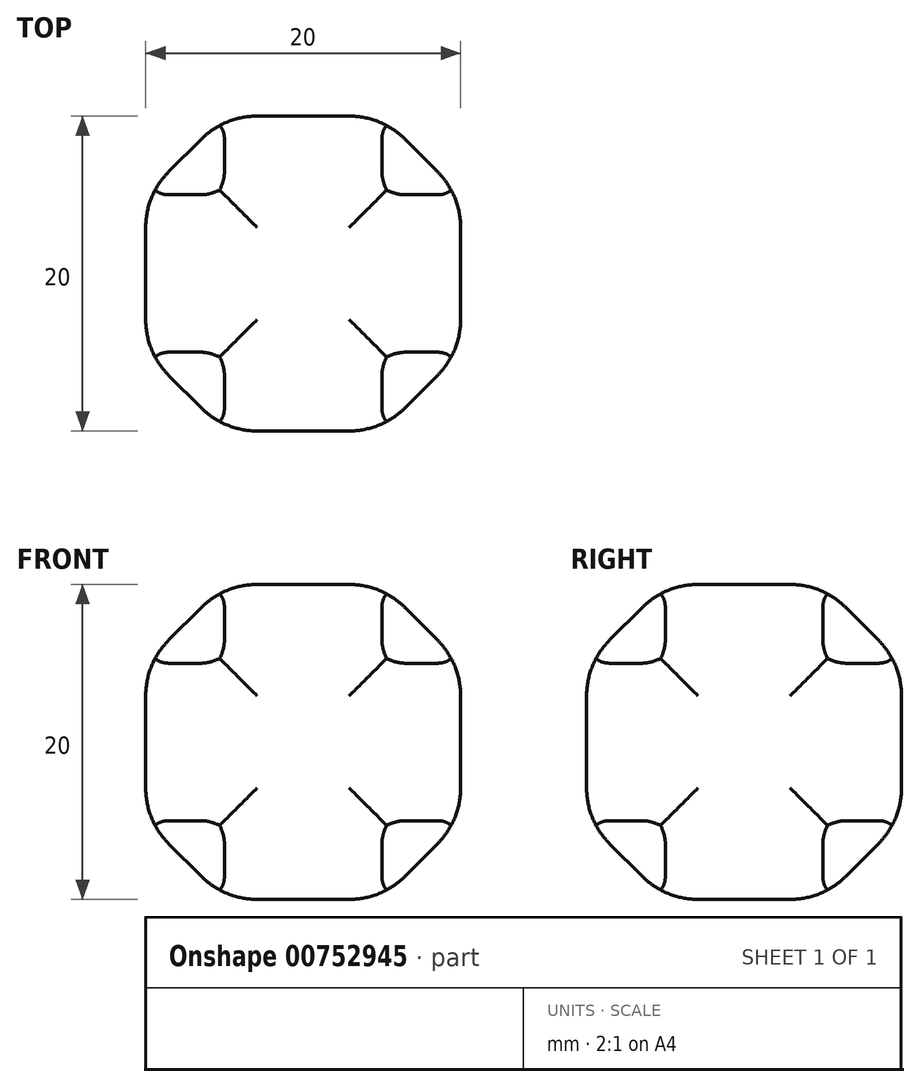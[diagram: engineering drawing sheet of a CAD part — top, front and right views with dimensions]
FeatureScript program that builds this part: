
annotation { "Feature Type Name" : "Feature", "Feature Type Description" : "" }
export const myFeature = defineFeature(function(context is Context, id is Id, definition is map)
    precondition{}
    {
        {
            var Q0;
            Q0=qCreatedBy(makeId("Top.planeOp"),FACE);
            var sketch = newSketch(context, id + "F0", { "sketchPlane" : qUnion([Q0])});
            skLineSegment(sketch, "E0.bottom", {"start": v(-1.4, 9.82) * mm, "end": v(18.6, 9.82) * mm});
            skLineSegment(sketch, "E0.top", {"start": v(-1.4, -10.18) * mm, "end": v(18.6, -10.18) * mm});
            skLineSegment(sketch, "E0.left", {"start": v(-1.4, 9.82) * mm, "end": v(-1.4, -10.18) * mm});
            skLineSegment(sketch, "E0.right", {"start": v(18.6, 9.82) * mm, "end": v(18.6, -10.18) * mm});
            skSolve(sketch);
        }
        {
            var Q0;
            Q0=makeQuery(id+"F0.imprint","IMPRINT",FACE,{"disambiguationData":[TD([[makeQuery(id+"F0.imprint","IMPRINT",EDGE,{"derivedFrom":sQuery(id+"F0.wireOp",EDGE,"E0.bottom")}),-1.0]])]});
            extrude(context, id + "F1", {"entities" : qUnion([Q0]), "depth" : 20 * mm, "offsetDistance" : 25 * mm});
        }
        {
            var Q0;
            Q0=makeQuery(id+"F1.opExtrude","CAP_EDGE",EDGE,{"disambiguationData":[OSD([sQuery(id+"F0.wireOp",EDGE,"E0.top")])],"isStart":false});
            var Q1;
            Q1=makeQuery(id+"F1.opExtrude","CAP_EDGE",EDGE,{"disambiguationData":[OSD([sQuery(id+"F0.wireOp",EDGE,"E0.right")])],"isStart":false});
            var Q2;
            Q2=makeQuery(id+"F1.opExtrude","CAP_EDGE",EDGE,{"disambiguationData":[OSD([sQuery(id+"F0.wireOp",EDGE,"E0.bottom")])],"isStart":false});
            var Q3;
            Q3=makeQuery(id+"F1.opExtrude","CAP_EDGE",EDGE,{"disambiguationData":[OSD([sQuery(id+"F0.wireOp",EDGE,"E0.left")])],"isStart":false});
            var Q4;
            Q4=makeQuery(id+"F1.opExtrude","CAP_EDGE",EDGE,{"disambiguationData":[OSD([sQuery(id+"F0.wireOp",EDGE,"E0.left")])],"isStart":true});
            var Q5;
            Q5=makeQuery(id+"F1.opExtrude","CAP_EDGE",EDGE,{"disambiguationData":[OSD([sQuery(id+"F0.wireOp",EDGE,"E0.bottom")])],"isStart":true});
            var Q6;
            Q6=makeQuery(id+"F1.opExtrude","CAP_EDGE",EDGE,{"disambiguationData":[OSD([sQuery(id+"F0.wireOp",EDGE,"E0.right")])],"isStart":true});
            var Q7;
            Q7=makeQuery(id+"F1.opExtrude","CAP_EDGE",EDGE,{"disambiguationData":[OSD([sQuery(id+"F0.wireOp",EDGE,"E0.top")])],"isStart":true});
            var Q8;
            Q8=makeQuery(id+"F1.opExtrude","SWEPT_EDGE",EDGE,{"disambiguationData":[OSD([sQuery(id+"F0.wireOp",EDGE,"E0.bottom"),sQuery(id+"F0.wireOp",EDGE,"E0.left")])]});
            var Q9;
            Q9=makeQuery(id+"F1.opExtrude","SWEPT_EDGE",EDGE,{"disambiguationData":[OSD([sQuery(id+"F0.wireOp",EDGE,"E0.bottom"),sQuery(id+"F0.wireOp",EDGE,"E0.right")])]});
            var Q10;
            Q10=makeQuery(id+"F1.opExtrude","SWEPT_EDGE",EDGE,{"disambiguationData":[OSD([sQuery(id+"F0.wireOp",EDGE,"E0.top"),sQuery(id+"F0.wireOp",EDGE,"E0.right")])]});
            var Q11;
            Q11=makeQuery(id+"F1.opExtrude","SWEPT_EDGE",EDGE,{"disambiguationData":[OSD([sQuery(id+"F0.wireOp",EDGE,"E0.top"),sQuery(id+"F0.wireOp",EDGE,"E0.left")])]});
            chamfer(context, id + "F2", {"entities" : qUnion([Q0, Q1, Q2, Q3, Q4, Q5, Q6, Q7, Q8, Q9, Q10, Q11]), "width" : 5 * mm, "tangentPropagation" : true});
        }
        {
            var Q0;
            {var subQ0=sQuery(id+"F0.wireOp",EDGE,"E0.right");Q0=makeQuery(id+"F2.opChamfer","BLEND_EDGE",EDGE,{"blendedFrom":[makeQuery(id+"F1.opExtrude","CAP_EDGE",EDGE,{"disambiguationData":[OSD([subQ0])],"isStart":true}),makeQuery(id+"F1.opExtrude","CAP_FACE",FACE,{"disambiguationData":[OSD([sQuery(id+"F0.wireOp",EDGE,"E0.bottom"),sQuery(id+"F0.wireOp",EDGE,"E0.top"),sQuery(id+"F0.wireOp",EDGE,"E0.left"),subQ0])],"isStart":true})],"blendedInto":[makeQuery(id+"F1.opExtrude","CAP_FACE",FACE,{"disambiguationData":[OSD([sQuery(id+"F0.wireOp",EDGE,"E0.bottom"),sQuery(id+"F0.wireOp",EDGE,"E0.top"),sQuery(id+"F0.wireOp",EDGE,"E0.left"),subQ0])],"isStart":true})]});}
            var Q1;
            {var subQ0=sQuery(id+"F0.wireOp",EDGE,"E0.right");Q1=makeQuery(id+"F2.opChamfer","BLEND_EDGE",EDGE,{"blendedFrom":[makeQuery(id+"F1.opExtrude","CAP_EDGE",EDGE,{"disambiguationData":[OSD([subQ0])],"isStart":true}),makeQuery(id+"F1.opExtrude","SWEPT_FACE",FACE,{"disambiguationData":[OSD([subQ0])]})],"blendedInto":[makeQuery(id+"F1.opExtrude","SWEPT_FACE",FACE,{"disambiguationData":[OSD([subQ0])]})]});}
            var Q2;
            {var subQ0=sQuery(id+"F0.wireOp",EDGE,"E0.right");Q2=makeQuery(id+"F2.opChamfer","BLEND_EDGE",EDGE,{"blendedFrom":[makeQuery(id+"F1.opExtrude","CAP_EDGE",EDGE,{"disambiguationData":[OSD([subQ0])],"isStart":false}),makeQuery(id+"F1.opExtrude","SWEPT_FACE",FACE,{"disambiguationData":[OSD([subQ0])]})],"blendedInto":[makeQuery(id+"F1.opExtrude","SWEPT_FACE",FACE,{"disambiguationData":[OSD([subQ0])]})]});}
            var Q3;
            {var subQ0=sQuery(id+"F0.wireOp",EDGE,"E0.right");Q3=makeQuery(id+"F2.opChamfer","BLEND_EDGE",EDGE,{"blendedFrom":[makeQuery(id+"F1.opExtrude","CAP_EDGE",EDGE,{"disambiguationData":[OSD([subQ0])],"isStart":false}),makeQuery(id+"F1.opExtrude","CAP_FACE",FACE,{"disambiguationData":[OSD([sQuery(id+"F0.wireOp",EDGE,"E0.bottom"),sQuery(id+"F0.wireOp",EDGE,"E0.top"),sQuery(id+"F0.wireOp",EDGE,"E0.left"),subQ0])],"isStart":false})],"blendedInto":[makeQuery(id+"F1.opExtrude","CAP_FACE",FACE,{"disambiguationData":[OSD([sQuery(id+"F0.wireOp",EDGE,"E0.bottom"),sQuery(id+"F0.wireOp",EDGE,"E0.top"),sQuery(id+"F0.wireOp",EDGE,"E0.left"),subQ0])],"isStart":false})]});}
            var Q4;
            {var subQ0=sQuery(id+"F0.wireOp",EDGE,"E0.left");Q4=makeQuery(id+"F2.opChamfer","BLEND_EDGE",EDGE,{"blendedFrom":[makeQuery(id+"F1.opExtrude","CAP_EDGE",EDGE,{"disambiguationData":[OSD([subQ0])],"isStart":false}),makeQuery(id+"F1.opExtrude","CAP_FACE",FACE,{"disambiguationData":[OSD([sQuery(id+"F0.wireOp",EDGE,"E0.bottom"),sQuery(id+"F0.wireOp",EDGE,"E0.top"),subQ0,sQuery(id+"F0.wireOp",EDGE,"E0.right")])],"isStart":false})],"blendedInto":[makeQuery(id+"F1.opExtrude","CAP_FACE",FACE,{"disambiguationData":[OSD([sQuery(id+"F0.wireOp",EDGE,"E0.bottom"),sQuery(id+"F0.wireOp",EDGE,"E0.top"),subQ0,sQuery(id+"F0.wireOp",EDGE,"E0.right")])],"isStart":false})]});}
            var Q5;
            {var subQ0=sQuery(id+"F0.wireOp",EDGE,"E0.left");Q5=makeQuery(id+"F2.opChamfer","BLEND_EDGE",EDGE,{"blendedFrom":[makeQuery(id+"F1.opExtrude","CAP_EDGE",EDGE,{"disambiguationData":[OSD([subQ0])],"isStart":false}),makeQuery(id+"F1.opExtrude","SWEPT_FACE",FACE,{"disambiguationData":[OSD([subQ0])]})],"blendedInto":[makeQuery(id+"F1.opExtrude","SWEPT_FACE",FACE,{"disambiguationData":[OSD([subQ0])]})]});}
            var Q6;
            {var subQ0=sQuery(id+"F0.wireOp",EDGE,"E0.left");Q6=makeQuery(id+"F2.opChamfer","BLEND_EDGE",EDGE,{"blendedFrom":[makeQuery(id+"F1.opExtrude","CAP_EDGE",EDGE,{"disambiguationData":[OSD([subQ0])],"isStart":true}),makeQuery(id+"F1.opExtrude","SWEPT_FACE",FACE,{"disambiguationData":[OSD([subQ0])]})],"blendedInto":[makeQuery(id+"F1.opExtrude","SWEPT_FACE",FACE,{"disambiguationData":[OSD([subQ0])]})]});}
            var Q7;
            {var subQ0=sQuery(id+"F0.wireOp",EDGE,"E0.left");Q7=makeQuery(id+"F2.opChamfer","BLEND_EDGE",EDGE,{"blendedFrom":[makeQuery(id+"F1.opExtrude","CAP_EDGE",EDGE,{"disambiguationData":[OSD([subQ0])],"isStart":true}),makeQuery(id+"F1.opExtrude","CAP_FACE",FACE,{"disambiguationData":[OSD([sQuery(id+"F0.wireOp",EDGE,"E0.bottom"),sQuery(id+"F0.wireOp",EDGE,"E0.top"),subQ0,sQuery(id+"F0.wireOp",EDGE,"E0.right")])],"isStart":true})],"blendedInto":[makeQuery(id+"F1.opExtrude","CAP_FACE",FACE,{"disambiguationData":[OSD([sQuery(id+"F0.wireOp",EDGE,"E0.bottom"),sQuery(id+"F0.wireOp",EDGE,"E0.top"),subQ0,sQuery(id+"F0.wireOp",EDGE,"E0.right")])],"isStart":true})]});}
            var Q8;
            {var subQ0=sQuery(id+"F0.wireOp",EDGE,"E0.bottom");Q8=makeQuery(id+"F2.opChamfer","BLEND_EDGE",EDGE,{"blendedFrom":[makeQuery(id+"F1.opExtrude","CAP_EDGE",EDGE,{"disambiguationData":[OSD([subQ0])],"isStart":true}),makeQuery(id+"F1.opExtrude","SWEPT_FACE",FACE,{"disambiguationData":[OSD([subQ0])]})],"blendedInto":[makeQuery(id+"F1.opExtrude","SWEPT_FACE",FACE,{"disambiguationData":[OSD([subQ0])]})]});}
            var Q9;
            {var subQ0=sQuery(id+"F0.wireOp",EDGE,"E0.bottom");Q9=makeQuery(id+"F2.opChamfer","BLEND_EDGE",EDGE,{"blendedFrom":[makeQuery(id+"F1.opExtrude","CAP_EDGE",EDGE,{"disambiguationData":[OSD([subQ0])],"isStart":false}),makeQuery(id+"F1.opExtrude","SWEPT_FACE",FACE,{"disambiguationData":[OSD([subQ0])]})],"blendedInto":[makeQuery(id+"F1.opExtrude","SWEPT_FACE",FACE,{"disambiguationData":[OSD([subQ0])]})]});}
            var Q10;
            {var subQ0=sQuery(id+"F0.wireOp",EDGE,"E0.bottom");Q10=makeQuery(id+"F2.opChamfer","BLEND_EDGE",EDGE,{"blendedFrom":[makeQuery(id+"F1.opExtrude","CAP_EDGE",EDGE,{"disambiguationData":[OSD([subQ0])],"isStart":true}),makeQuery(id+"F1.opExtrude","CAP_FACE",FACE,{"disambiguationData":[OSD([subQ0,sQuery(id+"F0.wireOp",EDGE,"E0.top"),sQuery(id+"F0.wireOp",EDGE,"E0.left"),sQuery(id+"F0.wireOp",EDGE,"E0.right")])],"isStart":true})],"blendedInto":[makeQuery(id+"F1.opExtrude","CAP_FACE",FACE,{"disambiguationData":[OSD([subQ0,sQuery(id+"F0.wireOp",EDGE,"E0.top"),sQuery(id+"F0.wireOp",EDGE,"E0.left"),sQuery(id+"F0.wireOp",EDGE,"E0.right")])],"isStart":true})]});}
            var Q11;
            {var subQ0=sQuery(id+"F0.wireOp",EDGE,"E0.top");Q11=makeQuery(id+"F2.opChamfer","BLEND_EDGE",EDGE,{"blendedFrom":[makeQuery(id+"F1.opExtrude","CAP_EDGE",EDGE,{"disambiguationData":[OSD([subQ0])],"isStart":true}),makeQuery(id+"F1.opExtrude","CAP_FACE",FACE,{"disambiguationData":[OSD([sQuery(id+"F0.wireOp",EDGE,"E0.bottom"),subQ0,sQuery(id+"F0.wireOp",EDGE,"E0.left"),sQuery(id+"F0.wireOp",EDGE,"E0.right")])],"isStart":true})],"blendedInto":[makeQuery(id+"F1.opExtrude","CAP_FACE",FACE,{"disambiguationData":[OSD([sQuery(id+"F0.wireOp",EDGE,"E0.bottom"),subQ0,sQuery(id+"F0.wireOp",EDGE,"E0.left"),sQuery(id+"F0.wireOp",EDGE,"E0.right")])],"isStart":true})]});}
            var Q12;
            {var subQ0=sQuery(id+"F0.wireOp",EDGE,"E0.top");Q12=makeQuery(id+"F2.opChamfer","BLEND_EDGE",EDGE,{"blendedFrom":[makeQuery(id+"F1.opExtrude","CAP_EDGE",EDGE,{"disambiguationData":[OSD([subQ0])],"isStart":true}),makeQuery(id+"F1.opExtrude","SWEPT_FACE",FACE,{"disambiguationData":[OSD([subQ0])]})],"blendedInto":[makeQuery(id+"F1.opExtrude","SWEPT_FACE",FACE,{"disambiguationData":[OSD([subQ0])]})]});}
            var Q13;
            {var subQ0=sQuery(id+"F0.wireOp",EDGE,"E0.top");Q13=makeQuery(id+"F2.opChamfer","BLEND_EDGE",EDGE,{"blendedFrom":[makeQuery(id+"F1.opExtrude","CAP_EDGE",EDGE,{"disambiguationData":[OSD([subQ0])],"isStart":false}),makeQuery(id+"F1.opExtrude","SWEPT_FACE",FACE,{"disambiguationData":[OSD([subQ0])]})],"blendedInto":[makeQuery(id+"F1.opExtrude","SWEPT_FACE",FACE,{"disambiguationData":[OSD([subQ0])]})]});}
            var Q14;
            {var subQ0=sQuery(id+"F0.wireOp",EDGE,"E0.top");Q14=makeQuery(id+"F2.opChamfer","BLEND_EDGE",EDGE,{"blendedFrom":[makeQuery(id+"F1.opExtrude","CAP_EDGE",EDGE,{"disambiguationData":[OSD([subQ0])],"isStart":false}),makeQuery(id+"F1.opExtrude","CAP_FACE",FACE,{"disambiguationData":[OSD([sQuery(id+"F0.wireOp",EDGE,"E0.bottom"),subQ0,sQuery(id+"F0.wireOp",EDGE,"E0.left"),sQuery(id+"F0.wireOp",EDGE,"E0.right")])],"isStart":false})],"blendedInto":[makeQuery(id+"F1.opExtrude","CAP_FACE",FACE,{"disambiguationData":[OSD([sQuery(id+"F0.wireOp",EDGE,"E0.bottom"),subQ0,sQuery(id+"F0.wireOp",EDGE,"E0.left"),sQuery(id+"F0.wireOp",EDGE,"E0.right")])],"isStart":false})]});}
            var Q15;
            {var subQ0=sQuery(id+"F0.wireOp",EDGE,"E0.bottom");Q15=makeQuery(id+"F2.opChamfer","BLEND_EDGE",EDGE,{"blendedFrom":[makeQuery(id+"F1.opExtrude","CAP_EDGE",EDGE,{"disambiguationData":[OSD([subQ0])],"isStart":false}),makeQuery(id+"F1.opExtrude","CAP_FACE",FACE,{"disambiguationData":[OSD([subQ0,sQuery(id+"F0.wireOp",EDGE,"E0.top"),sQuery(id+"F0.wireOp",EDGE,"E0.left"),sQuery(id+"F0.wireOp",EDGE,"E0.right")])],"isStart":false})],"blendedInto":[makeQuery(id+"F1.opExtrude","CAP_FACE",FACE,{"disambiguationData":[OSD([subQ0,sQuery(id+"F0.wireOp",EDGE,"E0.top"),sQuery(id+"F0.wireOp",EDGE,"E0.left"),sQuery(id+"F0.wireOp",EDGE,"E0.right")])],"isStart":false})]});}
            var Q16;
            {var subQ0=sQuery(id+"F0.wireOp",EDGE,"E0.left");Q16=makeQuery(id+"F2.opChamfer","BLEND_EDGE",EDGE,{"blendedFrom":[makeQuery(id+"F1.opExtrude","SWEPT_EDGE",EDGE,{"disambiguationData":[OSD([sQuery(id+"F0.wireOp",EDGE,"E0.bottom"),subQ0])]}),makeQuery(id+"F1.opExtrude","SWEPT_FACE",FACE,{"disambiguationData":[OSD([subQ0])]})],"blendedInto":[makeQuery(id+"F1.opExtrude","SWEPT_FACE",FACE,{"disambiguationData":[OSD([subQ0])]})]});}
            var Q17;
            {var subQ0=sQuery(id+"F0.wireOp",EDGE,"E0.bottom");Q17=makeQuery(id+"F2.opChamfer","BLEND_EDGE",EDGE,{"blendedFrom":[makeQuery(id+"F1.opExtrude","SWEPT_EDGE",EDGE,{"disambiguationData":[OSD([subQ0,sQuery(id+"F0.wireOp",EDGE,"E0.left")])]}),makeQuery(id+"F1.opExtrude","SWEPT_FACE",FACE,{"disambiguationData":[OSD([subQ0])]})],"blendedInto":[makeQuery(id+"F1.opExtrude","SWEPT_FACE",FACE,{"disambiguationData":[OSD([subQ0])]})]});}
            var Q18;
            {var subQ0=sQuery(id+"F0.wireOp",EDGE,"E0.bottom");Q18=makeQuery(id+"F2.opChamfer","BLEND_EDGE",EDGE,{"blendedFrom":[makeQuery(id+"F1.opExtrude","SWEPT_EDGE",EDGE,{"disambiguationData":[OSD([subQ0,sQuery(id+"F0.wireOp",EDGE,"E0.right")])]}),makeQuery(id+"F1.opExtrude","SWEPT_FACE",FACE,{"disambiguationData":[OSD([subQ0])]})],"blendedInto":[makeQuery(id+"F1.opExtrude","SWEPT_FACE",FACE,{"disambiguationData":[OSD([subQ0])]})]});}
            var Q19;
            {var subQ0=sQuery(id+"F0.wireOp",EDGE,"E0.right");Q19=makeQuery(id+"F2.opChamfer","BLEND_EDGE",EDGE,{"blendedFrom":[makeQuery(id+"F1.opExtrude","SWEPT_EDGE",EDGE,{"disambiguationData":[OSD([sQuery(id+"F0.wireOp",EDGE,"E0.bottom"),subQ0])]}),makeQuery(id+"F1.opExtrude","SWEPT_FACE",FACE,{"disambiguationData":[OSD([subQ0])]})],"blendedInto":[makeQuery(id+"F1.opExtrude","SWEPT_FACE",FACE,{"disambiguationData":[OSD([subQ0])]})]});}
            var Q20;
            {var subQ0=sQuery(id+"F0.wireOp",EDGE,"E0.right");Q20=makeQuery(id+"F2.opChamfer","BLEND_EDGE",EDGE,{"blendedFrom":[makeQuery(id+"F1.opExtrude","SWEPT_EDGE",EDGE,{"disambiguationData":[OSD([sQuery(id+"F0.wireOp",EDGE,"E0.top"),subQ0])]}),makeQuery(id+"F1.opExtrude","SWEPT_FACE",FACE,{"disambiguationData":[OSD([subQ0])]})],"blendedInto":[makeQuery(id+"F1.opExtrude","SWEPT_FACE",FACE,{"disambiguationData":[OSD([subQ0])]})]});}
            var Q21;
            {var subQ0=sQuery(id+"F0.wireOp",EDGE,"E0.top");Q21=makeQuery(id+"F2.opChamfer","BLEND_EDGE",EDGE,{"blendedFrom":[makeQuery(id+"F1.opExtrude","SWEPT_EDGE",EDGE,{"disambiguationData":[OSD([subQ0,sQuery(id+"F0.wireOp",EDGE,"E0.right")])]}),makeQuery(id+"F1.opExtrude","SWEPT_FACE",FACE,{"disambiguationData":[OSD([subQ0])]})],"blendedInto":[makeQuery(id+"F1.opExtrude","SWEPT_FACE",FACE,{"disambiguationData":[OSD([subQ0])]})]});}
            var Q22;
            {var subQ0=sQuery(id+"F0.wireOp",EDGE,"E0.top");Q22=makeQuery(id+"F2.opChamfer","BLEND_EDGE",EDGE,{"blendedFrom":[makeQuery(id+"F1.opExtrude","SWEPT_EDGE",EDGE,{"disambiguationData":[OSD([subQ0,sQuery(id+"F0.wireOp",EDGE,"E0.left")])]}),makeQuery(id+"F1.opExtrude","SWEPT_FACE",FACE,{"disambiguationData":[OSD([subQ0])]})],"blendedInto":[makeQuery(id+"F1.opExtrude","SWEPT_FACE",FACE,{"disambiguationData":[OSD([subQ0])]})]});}
            var Q23;
            {var subQ0=sQuery(id+"F0.wireOp",EDGE,"E0.left");Q23=makeQuery(id+"F2.opChamfer","BLEND_EDGE",EDGE,{"blendedFrom":[makeQuery(id+"F1.opExtrude","SWEPT_EDGE",EDGE,{"disambiguationData":[OSD([sQuery(id+"F0.wireOp",EDGE,"E0.top"),subQ0])]}),makeQuery(id+"F1.opExtrude","SWEPT_FACE",FACE,{"disambiguationData":[OSD([subQ0])]})],"blendedInto":[makeQuery(id+"F1.opExtrude","SWEPT_FACE",FACE,{"disambiguationData":[OSD([subQ0])]})]});}
            fillet(context, id + "F3", {"entities" : qUnion([Q0, Q1, Q2, Q3, Q4, Q5, Q6, Q7, Q8, Q9, Q10, Q11, Q12, Q13, Q14, Q15, Q16, Q17, Q18, Q19, Q20, Q21, Q22, Q23]), "radius" : 5 * mm, "tangentPropagation" : true, "allowEdgeOverflow" : false});
        }
    });
